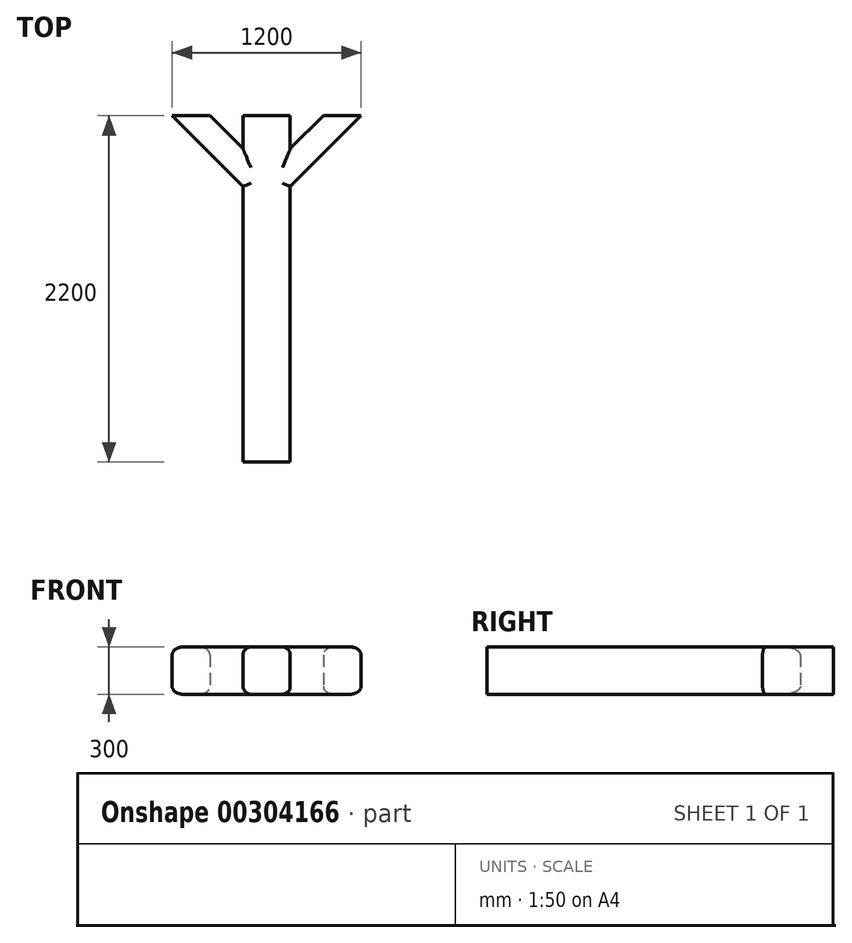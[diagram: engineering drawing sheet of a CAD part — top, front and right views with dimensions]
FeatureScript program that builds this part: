
annotation { "Feature Type Name" : "Feature", "Feature Type Description" : "" }
export const myFeature = defineFeature(function(context is Context, id is Id, definition is map)
    precondition{}
    {
        {
            var Q0;
            Q0=qCreatedBy(makeId("Top.planeOp"),FACE);
            var sketch = newSketch(context, id + "F0", { "sketchPlane" : qUnion([Q0])});
            skLineSegment(sketch, "E0", {"start": v(-260.88, -1120.02) * mm, "end": v(39.12, -1120.02) * mm});
            skLineSegment(sketch, "E1", {"start": v(39.12, -1120.02) * mm, "end": v(39.12, 629.98) * mm});
            skLineSegment(sketch, "E2", {"start": v(39.12, 629.98) * mm, "end": v(489.12, 1079.98) * mm});
            skLineSegment(sketch, "E3", {"start": v(489.12, 1079.98) * mm, "end": v(249.12, 1079.98) * mm});
            skLineSegment(sketch, "E4", {"start": v(249.12, 1079.98) * mm, "end": v(39.12, 869.98) * mm});
            skLineSegment(sketch, "E5", {"start": v(39.12, 869.98) * mm, "end": v(39.12, 1079.98) * mm});
            skLineSegment(sketch, "E6", {"start": v(39.12, 1079.98) * mm, "end": v(-260.88, 1079.98) * mm});
            skLineSegment(sketch, "E7", {"start": v(-260.88, 1079.98) * mm, "end": v(-260.88, 869.98) * mm});
            skLineSegment(sketch, "E8", {"start": v(-260.88, 869.98) * mm, "end": v(-470.88, 1079.98) * mm});
            skLineSegment(sketch, "E9", {"start": v(-470.88, 1079.98) * mm, "end": v(-710.88, 1079.98) * mm});
            skLineSegment(sketch, "E10", {"start": v(-710.88, 1079.98) * mm, "end": v(-260.88, 629.98) * mm});
            skLineSegment(sketch, "E11", {"start": v(-260.88, 629.98) * mm, "end": v(-260.88, -1120.02) * mm});
            skSolve(sketch);
        }
        {
            var Q0;
            Q0=makeQuery(id+"F0.imprint","IMPRINT",FACE,{"disambiguationData":[TD([[makeQuery(id+"F0.imprint","IMPRINT",EDGE,{"derivedFrom":sQuery(id+"F0.wireOp",EDGE,"E0")}),1.0]])]});
            extrude(context, id + "F1", {"entities" : qUnion([Q0]), "depth" : 300 * mm});
        }
        {
            var Q0;
            Q0=makeQuery(id+"F1.opExtrude","CAP_EDGE",EDGE,{"disambiguationData":[OSD([sQuery(id+"F0.wireOp",EDGE,"E11")])],"isStart":false});
            var Q1;
            Q1=makeQuery(id+"F1.opExtrude","CAP_EDGE",EDGE,{"disambiguationData":[OSD([sQuery(id+"F0.wireOp",EDGE,"E1")])],"isStart":false});
            var Q2;
            Q2=makeQuery(id+"F1.opExtrude","CAP_EDGE",EDGE,{"disambiguationData":[OSD([sQuery(id+"F0.wireOp",EDGE,"E1")])],"isStart":true});
            var Q3;
            Q3=makeQuery(id+"F1.opExtrude","CAP_EDGE",EDGE,{"disambiguationData":[OSD([sQuery(id+"F0.wireOp",EDGE,"E11")])],"isStart":true});
            var Q4;
            Q4=makeQuery(id+"F1.opExtrude","CAP_EDGE",EDGE,{"disambiguationData":[OSD([sQuery(id+"F0.wireOp",EDGE,"E5")])],"isStart":true});
            var Q5;
            Q5=makeQuery(id+"F1.opExtrude","CAP_EDGE",EDGE,{"disambiguationData":[OSD([sQuery(id+"F0.wireOp",EDGE,"E7")])],"isStart":true});
            var Q6;
            Q6=makeQuery(id+"F1.opExtrude","CAP_EDGE",EDGE,{"disambiguationData":[OSD([sQuery(id+"F0.wireOp",EDGE,"E5")])],"isStart":false});
            var Q7;
            Q7=makeQuery(id+"F1.opExtrude","CAP_EDGE",EDGE,{"disambiguationData":[OSD([sQuery(id+"F0.wireOp",EDGE,"E7")])],"isStart":false});
            var Q8;
            Q8=makeQuery(id+"F1.opExtrude","CAP_EDGE",EDGE,{"disambiguationData":[OSD([sQuery(id+"F0.wireOp",EDGE,"E8")])],"isStart":false});
            var Q9;
            Q9=makeQuery(id+"F1.opExtrude","CAP_EDGE",EDGE,{"disambiguationData":[OSD([sQuery(id+"F0.wireOp",EDGE,"E10")])],"isStart":false});
            var Q10;
            Q10=makeQuery(id+"F1.opExtrude","CAP_EDGE",EDGE,{"disambiguationData":[OSD([sQuery(id+"F0.wireOp",EDGE,"E2")])],"isStart":false});
            var Q11;
            Q11=makeQuery(id+"F1.opExtrude","CAP_EDGE",EDGE,{"disambiguationData":[OSD([sQuery(id+"F0.wireOp",EDGE,"E2")])],"isStart":true});
            var Q12;
            Q12=makeQuery(id+"F1.opExtrude","CAP_EDGE",EDGE,{"disambiguationData":[OSD([sQuery(id+"F0.wireOp",EDGE,"E4")])],"isStart":true});
            var Q13;
            Q13=makeQuery(id+"F1.opExtrude","CAP_EDGE",EDGE,{"disambiguationData":[OSD([sQuery(id+"F0.wireOp",EDGE,"E8")])],"isStart":true});
            var Q14;
            Q14=makeQuery(id+"F1.opExtrude","CAP_EDGE",EDGE,{"disambiguationData":[OSD([sQuery(id+"F0.wireOp",EDGE,"E10")])],"isStart":true});
            var Q15;
            Q15=makeQuery(id+"F1.opExtrude","CAP_EDGE",EDGE,{"disambiguationData":[OSD([sQuery(id+"F0.wireOp",EDGE,"E4")])],"isStart":false});
            fillet(context, id + "F2", {"entities" : qUnion([Q0, Q1, Q2, Q3, Q4, Q5, Q6, Q7, Q8, Q9, Q10, Q11, Q12, Q13, Q14, Q15]), "radius" : 50 * mm, "tangentPropagation" : true, "allowEdgeOverflow" : false});
        }
    });
